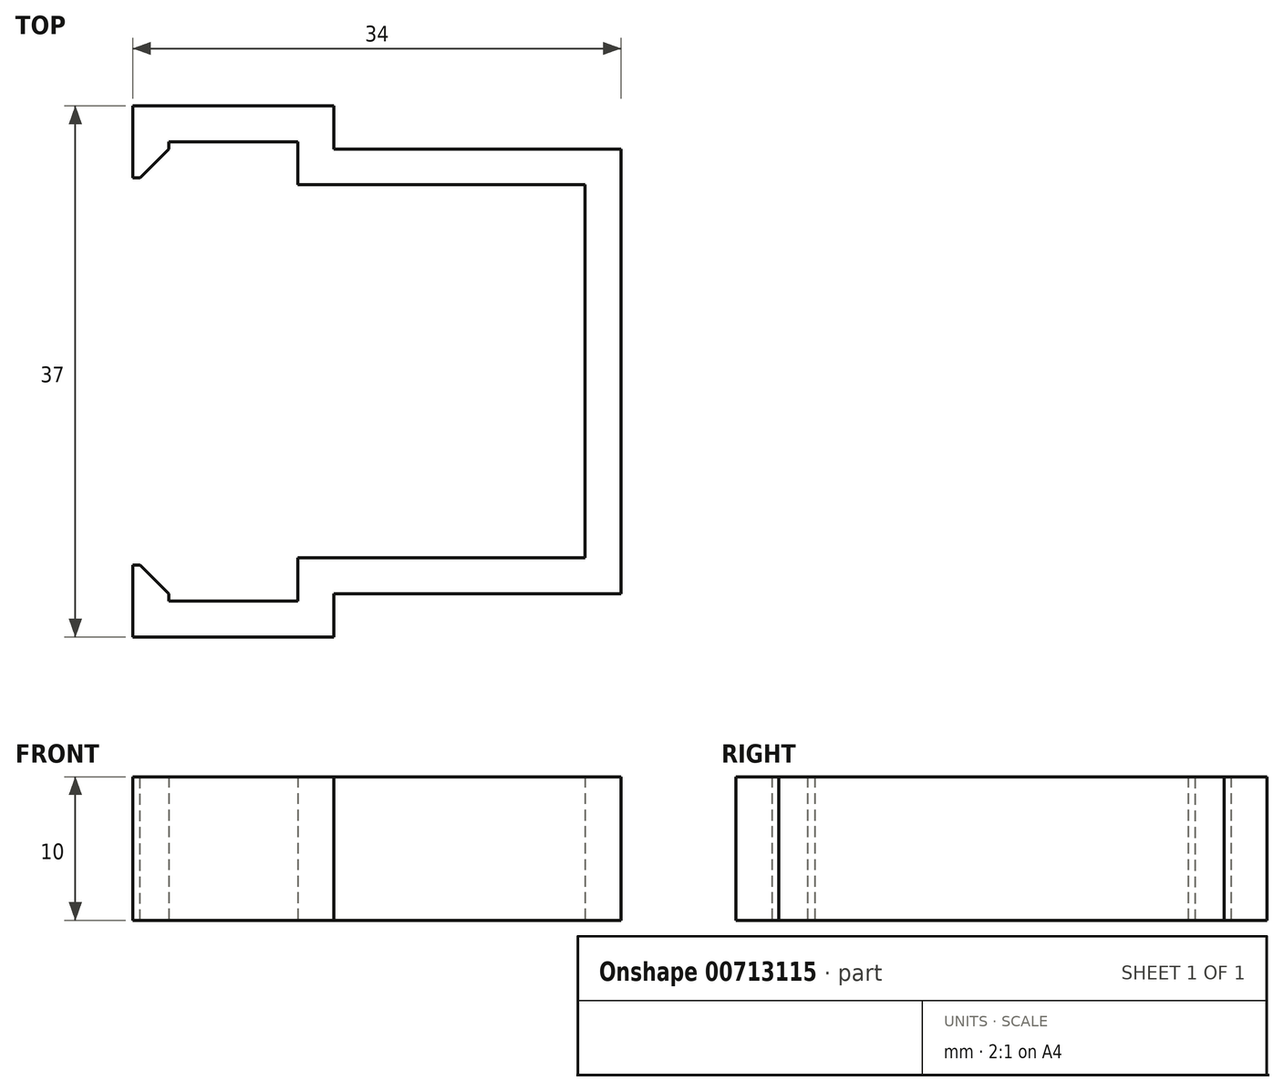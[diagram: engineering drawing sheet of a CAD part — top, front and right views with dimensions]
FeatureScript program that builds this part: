
annotation { "Feature Type Name" : "Feature", "Feature Type Description" : "" }
export const myFeature = defineFeature(function(context is Context, id is Id, definition is map)
    precondition{}
    {
        {
            var Q0;
            Q0=qCreatedBy(makeId("Top.planeOp"),FACE);
            var sketch = newSketch(context, id + "F0", { "sketchPlane" : qUnion([Q0])});
            skLineSegment(sketch, "E0.bottom", {"start": v(10, 13) * mm, "end": v(-10, 13) * mm});
            skLineSegment(sketch, "E0.top", {"start": v(10, -13) * mm, "end": v(-10, -13) * mm});
            skLineSegment(sketch, "E0.left", {"start": v(10, 13) * mm, "end": v(10, -13) * mm});
            skPoint(sketch, "E0.middle", {"position": v(0, 0) * mm});
            skLineSegment(sketch, "E1.bottom", {"start": v(-19, 16) * mm, "end": v(-10, 16) * mm});
            skLineSegment(sketch, "E1.top", {"start": v(-19, -16) * mm, "end": v(-10, -16) * mm});
            skLineSegment(sketch, "E2", {"start": v(-10, 13) * mm, "end": v(-10, 16) * mm});
            skLineSegment(sketch, "E3", {"start": v(-10, -13) * mm, "end": v(-10, -16) * mm});
            skLineSegment(sketch, "E4.0", {"start": v(-19, 18.5) * mm, "end": v(-7.5, 18.5) * mm});
            skLineSegment(sketch, "E4.1", {"start": v(-7.5, 15.5) * mm, "end": v(-7.5, 18.5) * mm});
            skLineSegment(sketch, "E4.2", {"start": v(12.5, 15.5) * mm, "end": v(-7.5, 15.5) * mm});
            skLineSegment(sketch, "E4.3", {"start": v(-19, -18.5) * mm, "end": v(-7.5, -18.5) * mm});
            skLineSegment(sketch, "E4.4", {"start": v(-7.5, -15.5) * mm, "end": v(-7.5, -18.5) * mm});
            skLineSegment(sketch, "E4.5", {"start": v(12.5, -15.5) * mm, "end": v(-7.5, -15.5) * mm});
            skLineSegment(sketch, "E4.6", {"start": v(12.5, 15.5) * mm, "end": v(12.5, -15.5) * mm});
            skLineSegment(sketch, "E5.bottom", {"start": v(-19, 18.5) * mm, "end": v(-21.5, 18.5) * mm});
            skLineSegment(sketch, "E5.top", {"start": v(-19, 13.5) * mm, "end": v(-21.5, 13.5) * mm});
            skLineSegment(sketch, "E5.left", {"start": v(-19, 16) * mm, "end": v(-19, 13.5) * mm});
            skLineSegment(sketch, "E5.right", {"start": v(-21.5, 18.5) * mm, "end": v(-21.5, 13.5) * mm});
            skLineSegment(sketch, "E6.bottom", {"start": v(-19, -18.5) * mm, "end": v(-21.5, -18.5) * mm});
            skLineSegment(sketch, "E6.top", {"start": v(-19, -13.5) * mm, "end": v(-21.5, -13.5) * mm});
            skLineSegment(sketch, "E6.left", {"start": v(-19, -16) * mm, "end": v(-19, -13.5) * mm});
            skLineSegment(sketch, "E6.right", {"start": v(-21.5, -18.5) * mm, "end": v(-21.5, -13.5) * mm});
            skSolve(sketch);
        }
        {
            var Q0;
            Q0=makeQuery(id+"F0.imprint","IMPRINT",FACE,{"disambiguationData":[TD([[makeQuery(id+"F0.imprint","IMPRINT",EDGE,{"derivedFrom":sQuery(id+"F0.wireOp",EDGE,"E0.bottom")}),-1.0]])]});
            extrude(context, id + "F1", {"entities" : qUnion([Q0]), "depth" : 10 * mm, "offsetDistance" : 25 * mm});
        }
        {
            var Q0;
            Q0=makeQuery(id+"F1.opExtrude","SWEPT_EDGE",EDGE,{"disambiguationData":[OSD([sQuery(id+"F0.wireOp",EDGE,"E5.top"),sQuery(id+"F0.wireOp",EDGE,"E5.left")])]});
            var Q1;
            Q1=makeQuery(id+"F1.opExtrude","SWEPT_EDGE",EDGE,{"disambiguationData":[OSD([sQuery(id+"F0.wireOp",EDGE,"E6.top"),sQuery(id+"F0.wireOp",EDGE,"E6.left")])]});
            chamfer(context, id + "F2", {"entities" : qUnion([Q0, Q1]), "width" : 2 * mm, "tangentPropagation" : true});
        }
    });
